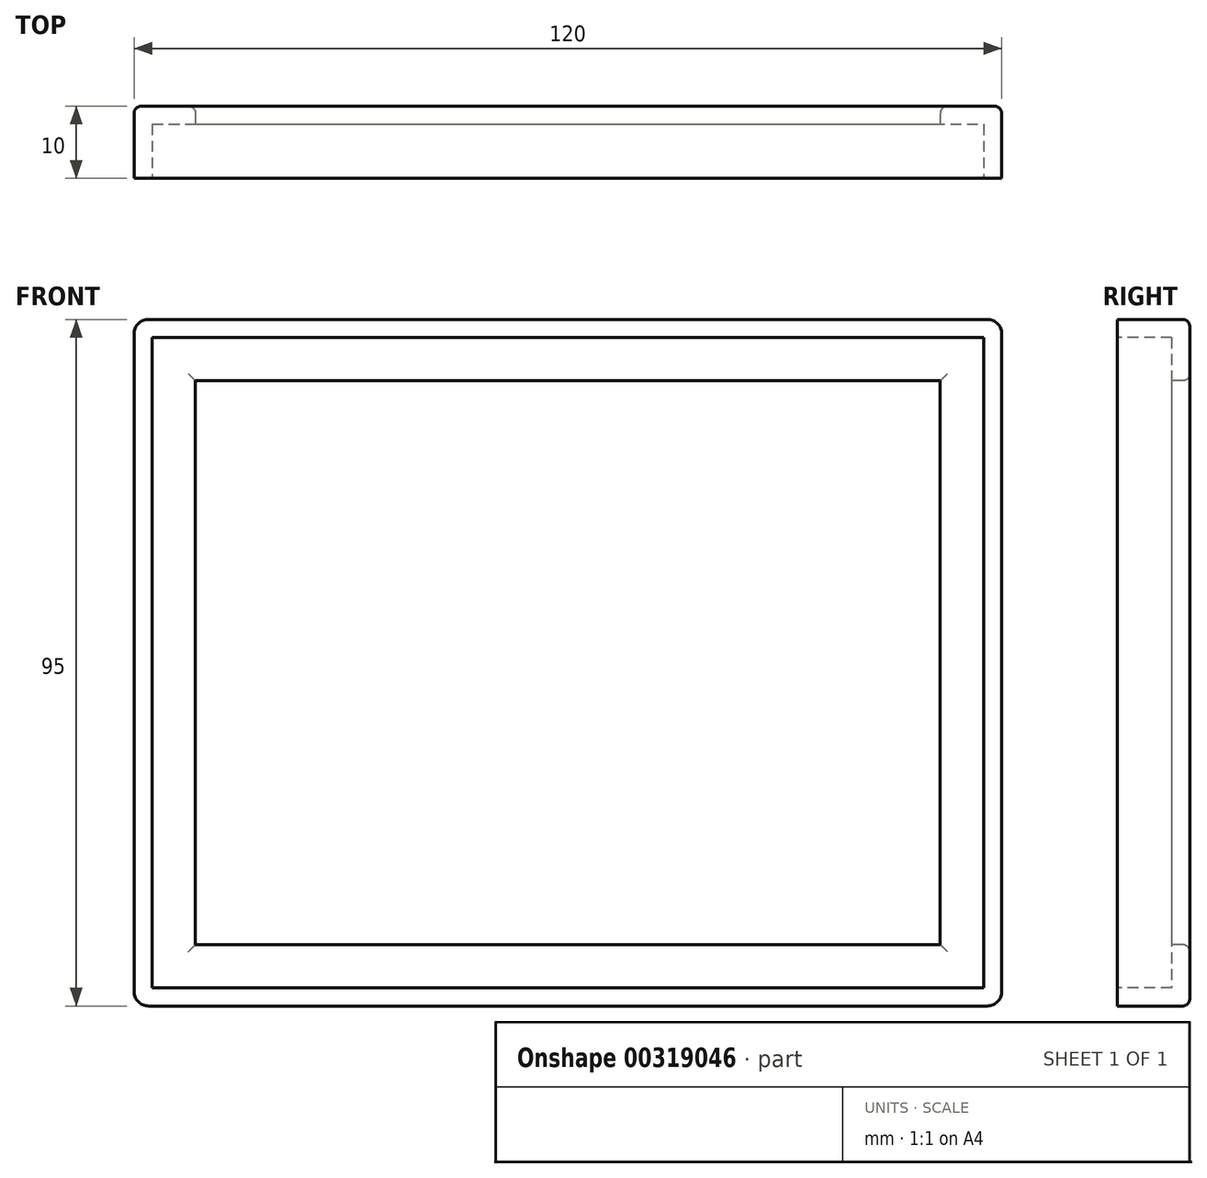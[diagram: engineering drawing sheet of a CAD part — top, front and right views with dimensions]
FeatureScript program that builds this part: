
annotation { "Feature Type Name" : "Feature", "Feature Type Description" : "" }
export const myFeature = defineFeature(function(context is Context, id is Id, definition is map)
    precondition{}
    {
        {
            var Q0;
            Q0=qCreatedBy(makeId("Front.planeOp"),FACE);
            var sketch = newSketch(context, id + "F0", { "sketchPlane" : qUnion([Q0])});
            skLineSegment(sketch, "E0.bottom", {"start": v(-60, 47.5) * mm, "end": v(60, 47.5) * mm});
            skLineSegment(sketch, "E0.top", {"start": v(-60, -47.5) * mm, "end": v(60, -47.5) * mm});
            skLineSegment(sketch, "E0.left", {"start": v(-60, 47.5) * mm, "end": v(-60, -47.5) * mm});
            skLineSegment(sketch, "E0.right", {"start": v(60, 47.5) * mm, "end": v(60, -47.5) * mm});
            skSolve(sketch);
        }
        {
            var Q0;
            Q0=makeQuery(id+"F0.imprint","IMPRINT",FACE,{"disambiguationData":[TD([[makeQuery(id+"F0.imprint","IMPRINT",EDGE,{"derivedFrom":sQuery(id+"F0.wireOp",EDGE,"E0.bottom")}),-1.0]])]});
            extrude(context, id + "F1", {"entities" : qUnion([Q0]), "depth" : 10 * mm});
        }
        {
            var Q0;
            Q0=makeQuery(id+"F1.opExtrude","CAP_FACE",FACE,{"disambiguationData":[OSD([sQuery(id+"F0.wireOp",EDGE,"E0.bottom"),sQuery(id+"F0.wireOp",EDGE,"E0.top"),sQuery(id+"F0.wireOp",EDGE,"E0.left"),sQuery(id+"F0.wireOp",EDGE,"E0.right")])],"isStart":false});
            var sketch = newSketch(context, id + "F2", { "sketchPlane" : qUnion([Q0])});
            skLineSegment(sketch, "E1.bottom", {"start": v(-57.5, 45) * mm, "end": v(57.5, 45) * mm});
            skLineSegment(sketch, "E1.top", {"start": v(-57.5, -45) * mm, "end": v(57.5, -45) * mm});
            skLineSegment(sketch, "E1.left", {"start": v(-57.5, 45) * mm, "end": v(-57.5, -45) * mm});
            skLineSegment(sketch, "E1.right", {"start": v(57.5, 45) * mm, "end": v(57.5, -45) * mm});
            skSolve(sketch);
        }
        {
            var Q0;
            Q0=makeQuery(id+"F2.imprint","IMPRINT",FACE,{"disambiguationData":[TD([[makeQuery(id+"F2.imprint","IMPRINT",EDGE,{"derivedFrom":sQuery(id+"F2.wireOp",EDGE,"E1.bottom")}),-1.0]])]});
            extrude(context, id + "F3", {"entities" : qUnion([Q0]), "operationType" : NewBodyOperationType.REMOVE, "oppositeDirection" : true, "depth" : 7.5 * mm});
        }
        {
            var Q0;
            Q0=makeQuery(id+"F3.boolean.opBoolean","COPY",FACE,{"derivedFrom":makeQuery(id+"F3.opExtrude","CAP_FACE",FACE,{"disambiguationData":[OSD([sQuery(id+"F2.wireOp",EDGE,"E1.bottom"),sQuery(id+"F2.wireOp",EDGE,"E1.top"),sQuery(id+"F2.wireOp",EDGE,"E1.left"),sQuery(id+"F2.wireOp",EDGE,"E1.right")])],"isStart":false})});
            var sketch = newSketch(context, id + "F4", { "sketchPlane" : qUnion([Q0])});
            skLineSegment(sketch, "E2.bottom", {"start": v(-51.5, 39) * mm, "end": v(51.5, 39) * mm});
            skLineSegment(sketch, "E2.top", {"start": v(-51.5, -39) * mm, "end": v(51.5, -39) * mm});
            skLineSegment(sketch, "E2.left", {"start": v(-51.5, 39) * mm, "end": v(-51.5, -39) * mm});
            skLineSegment(sketch, "E2.right", {"start": v(51.5, 39) * mm, "end": v(51.5, -39) * mm});
            skSolve(sketch);
        }
        {
            var Q0;
            Q0=makeQuery(id+"F4.imprint","IMPRINT",FACE,{"disambiguationData":[TD([[makeQuery(id+"F4.imprint","IMPRINT",EDGE,{"derivedFrom":sQuery(id+"F4.wireOp",EDGE,"E2.bottom")}),-1.0]])]});
            extrude(context, id + "F5", {"entities" : qUnion([Q0]), "operationType" : NewBodyOperationType.REMOVE, "endBound" : BoundingType.THROUGH_ALL, "oppositeDirection" : true, "depth" : 25 * mm});
        }
        {
            var Q0;
            Q0=makeQuery(id+"F1.opExtrude","SWEPT_EDGE",EDGE,{"disambiguationData":[OSD([sQuery(id+"F0.wireOp",EDGE,"E0.bottom"),sQuery(id+"F0.wireOp",EDGE,"E0.right")])]});
            var Q1;
            Q1=makeQuery(id+"F1.opExtrude","SWEPT_EDGE",EDGE,{"disambiguationData":[OSD([sQuery(id+"F0.wireOp",EDGE,"E0.top"),sQuery(id+"F0.wireOp",EDGE,"E0.right")])]});
            var Q2;
            Q2=makeQuery(id+"F1.opExtrude","SWEPT_EDGE",EDGE,{"disambiguationData":[OSD([sQuery(id+"F0.wireOp",EDGE,"E0.top"),sQuery(id+"F0.wireOp",EDGE,"E0.left")])]});
            var Q3;
            Q3=makeQuery(id+"F1.opExtrude","SWEPT_EDGE",EDGE,{"disambiguationData":[OSD([sQuery(id+"F0.wireOp",EDGE,"E0.bottom"),sQuery(id+"F0.wireOp",EDGE,"E0.left")])]});
            fillet(context, id + "F6", {"entities" : qUnion([Q0, Q1, Q2, Q3]), "radius" : 2 * mm, "tangentPropagation" : true, "allowEdgeOverflow" : false});
        }
        {
            var Q0;
            Q0=makeQuery(id+"F1.opExtrude","CAP_FACE",FACE,{"disambiguationData":[OSD([sQuery(id+"F0.wireOp",EDGE,"E0.bottom"),sQuery(id+"F0.wireOp",EDGE,"E0.top"),sQuery(id+"F0.wireOp",EDGE,"E0.left"),sQuery(id+"F0.wireOp",EDGE,"E0.right")])],"isStart":true});
            fillet(context, id + "F7", {"entities" : qUnion([Q0]), "radius" : 1 * mm, "tangentPropagation" : true, "allowEdgeOverflow" : false});
        }
    });
